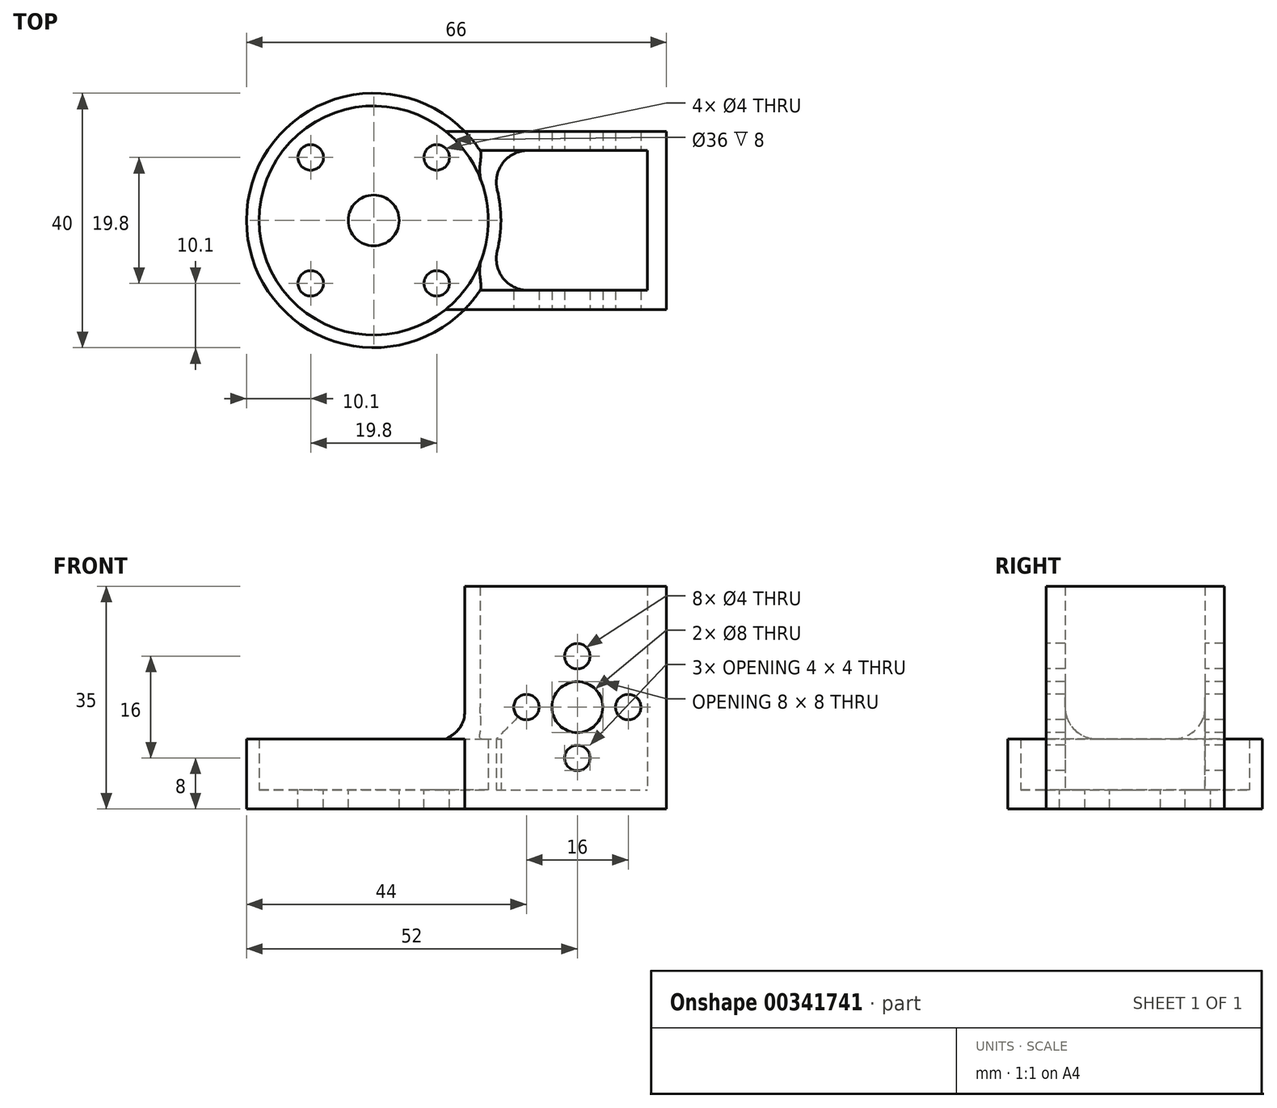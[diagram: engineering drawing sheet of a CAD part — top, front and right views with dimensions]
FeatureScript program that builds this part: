
annotation { "Feature Type Name" : "Feature", "Feature Type Description" : "" }
export const myFeature = defineFeature(function(context is Context, id is Id, definition is map)
    precondition{}
    {
        {
            var Q0;
            Q0=qCreatedBy(makeId("Top.planeOp"),FACE);
            var sketch = newSketch(context, id + "F0", { "sketchPlane" : qUnion([Q0])});
            skCircle(sketch, "E0", {"center": v(0, 0) * mm, "radius": 4 * mm});
            skCircle(sketch, "E1", {"center": v(0, 0) * mm, "radius": 14 * mm, "construction": true});
            skPoint(sketch, "E2", {"position": v(-9.9, 9.9) * mm});
            skLineSegment(sketch, "E3", {"start": v(0, 0) * mm, "end": v(-9.9, 9.9) * mm, "construction": true});
            skPoint(sketch, "E4.MirrorP", {"position": v(-9.9, -9.9) * mm});
            skPoint(sketch, "E5.MirrorP", {"position": v(9.9, 9.9) * mm});
            skPoint(sketch, "E6.MirrorP", {"position": v(9.9, -9.9) * mm});
            skCircle(sketch, "E7", {"center": v(-9.9, 9.9) * mm, "radius": 2 * mm});
            skCircle(sketch, "E8", {"center": v(9.9, 9.9) * mm, "radius": 2 * mm});
            skCircle(sketch, "E9", {"center": v(9.9, -9.9) * mm, "radius": 2 * mm});
            skCircle(sketch, "E10", {"center": v(-9.9, -9.9) * mm, "radius": 2 * mm});
            skCircle(sketch, "E11", {"center": v(0, 0) * mm, "radius": 18 * mm});
            skCircle(sketch, "E12", {"center": v(0, 0) * mm, "radius": 20 * mm});
            skLineSegment(sketch, "E13", {"start": v(46, 14) * mm, "end": v(46, -14) * mm});
            skLineSegment(sketch, "E14", {"start": v(14.28, 14) * mm, "end": v(46, 14) * mm});
            skLineSegment(sketch, "E15", {"start": v(32, 0) * mm, "end": v(0, 0) * mm, "construction": true});
            skLineSegment(sketch, "E16", {"start": v(46, 16) * mm, "end": v(46, -16) * mm, "construction": true});
            skLineSegment(sketch, "E17.MirrorCS", {"start": v(14.28, -14) * mm, "end": v(46, -14) * mm});
            skLineSegment(sketch, "E18.0", {"start": v(16.7, -11) * mm, "end": v(43, -11) * mm});
            skLineSegment(sketch, "E18.1", {"start": v(43, 11) * mm, "end": v(43, -11) * mm});
            skLineSegment(sketch, "E18.2", {"start": v(16.7, 11) * mm, "end": v(43, 11) * mm});
            skSolve(sketch);
        }
        {
            var Q0;
            Q0=makeQuery(id+"F0.imprint","IMPRINT",FACE,{"disambiguationData":[TD([[makeQuery(id+"F0.imprint","IMPRINT",EDGE,{"derivedFrom":sQuery(id+"F0.wireOp",EDGE,"E11")}),-1.0]])]});
            var Q1;
            Q1=makeQuery(id+"F0.imprint","IMPRINT",FACE,{"disambiguationData":[TD([[makeQuery(id+"F0.imprint","IMPRINT",EDGE,{"derivedFrom":sQuery(id+"F0.wireOp",EDGE,"E0")}),-1.0]])]});
            var Q2;
            Q2=makeQuery(id+"F0.imprint","IMPRINT",FACE,{"disambiguationData":[TD([[makeQuery(id+"F0.imprint","IMPRINT",EDGE,{"derivedFrom":sQuery(id+"F0.wireOp",EDGE,"E13")}),-1.0]])]});
            var Q3;
            {var subQ0=sQuery(id+"F0.wireOp",EDGE,"E18.0");Q3=makeQuery(id+"F0.imprint","IMPRINT",FACE,{"disambiguationData":[TD([[makeQuery(id+"F0.imprint","IMPRINT",EDGE,{"derivedFrom":subQ0}),1.0]])]});}
            extrude(context, id + "F1", {"entities" : qUnion([Q0, Q1, Q2, Q3]), "oppositeDirection" : true, "depth" : 3 * mm});
        }
        {
            var Q0;
            Q0=makeQuery(id+"F0.imprint","IMPRINT",FACE,{"disambiguationData":[TD([[makeQuery(id+"F0.imprint","IMPRINT",EDGE,{"derivedFrom":sQuery(id+"F0.wireOp",EDGE,"E11")}),-1.0]])]});
            var Q1;
            Q1=makeQuery(id+"F0.imprint","IMPRINT",FACE,{"disambiguationData":[TD([[makeQuery(id+"F0.imprint","IMPRINT",EDGE,{"derivedFrom":sQuery(id+"F0.wireOp",EDGE,"E13")}),-1.0]])]});
            extrude(context, id + "F2", {"entities" : qUnion([Q0, Q1]), "operationType" : NewBodyOperationType.ADD, "depth" : 8 * mm});
        }
        {
            var Q0;
            Q0=makeQuery(id+"F0.imprint","IMPRINT",FACE,{"disambiguationData":[TD([[makeQuery(id+"F0.imprint","IMPRINT",EDGE,{"derivedFrom":sQuery(id+"F0.wireOp",EDGE,"E13")}),-1.0]])]});
            extrude(context, id + "F3", {"entities" : qUnion([Q0]), "operationType" : NewBodyOperationType.ADD, "depth" : 32 * mm});
        }
        {
            var Q0;
            Q0=qCreatedBy(makeId("Front.planeOp"),FACE);
            var sketch = newSketch(context, id + "F4", { "sketchPlane" : qUnion([Q0])});
            skPoint(sketch, "E19.0", {"position": v(32, 0) * mm});
            skCircle(sketch, "E20", {"center": v(32, 13) * mm, "radius": 4 * mm});
            skCircle(sketch, "E21", {"center": v(32, 5) * mm, "radius": 2 * mm});
            skCircle(sketch, "E22.1.0", {"center": v(40, 13) * mm, "radius": 2 * mm});
            skCircle(sketch, "E22.2.0", {"center": v(32, 21) * mm, "radius": 2 * mm});
            skCircle(sketch, "E22.3.0", {"center": v(24, 13) * mm, "radius": 2 * mm});
            skSolve(sketch);
        }
        {
            var Q0;
            Q0=makeQuery(id+"F4.imprint","IMPRINT",FACE,{"disambiguationData":[TD([[makeQuery(id+"F4.imprint","IMPRINT",EDGE,{"derivedFrom":sQuery(id+"F4.wireOp",EDGE,"E22.2.0")}),1.0]])]});
            var Q1;
            Q1=makeQuery(id+"F4.imprint","IMPRINT",FACE,{"disambiguationData":[TD([[makeQuery(id+"F4.imprint","IMPRINT",EDGE,{"derivedFrom":sQuery(id+"F4.wireOp",EDGE,"E22.3.0")}),1.0]])]});
            var Q2;
            Q2=makeQuery(id+"F4.imprint","IMPRINT",FACE,{"disambiguationData":[TD([[makeQuery(id+"F4.imprint","IMPRINT",EDGE,{"derivedFrom":sQuery(id+"F4.wireOp",EDGE,"E20")}),1.0]])]});
            var Q3;
            Q3=makeQuery(id+"F4.imprint","IMPRINT",FACE,{"disambiguationData":[TD([[makeQuery(id+"F4.imprint","IMPRINT",EDGE,{"derivedFrom":sQuery(id+"F4.wireOp",EDGE,"E22.1.0")}),1.0]])]});
            var Q4;
            Q4=makeQuery(id+"F4.imprint","IMPRINT",FACE,{"disambiguationData":[TD([[makeQuery(id+"F4.imprint","IMPRINT",EDGE,{"derivedFrom":sQuery(id+"F4.wireOp",EDGE,"E21")}),1.0]])]});
            extrude(context, id + "F5", {"entities" : qUnion([Q0, Q1, Q2, Q3, Q4]), "operationType" : NewBodyOperationType.REMOVE, "endBound" : BoundingType.THROUGH_ALL, "oppositeDirection" : true, "depth" : 25 * mm, "hasSecondDirection" : true, "secondDirectionBound" : SecondDirectionBoundingType.THROUGH_ALL, "secondDirectionOppositeDirection" : false, "secondDirectionDepth" : 25 * mm});
        }
        {
            var Q0;
            Q0=makeQuery(id+"F2.opExtrude","SWEPT_EDGE",EDGE,{"disambiguationData":[OSD([sQuery(id+"F0.wireOp",EDGE,"E12"),sQuery(id+"F0.wireOp",EDGE,"E18.2")])]});
            var Q1;
            Q1=makeQuery(id+"F2.opExtrude","SWEPT_EDGE",EDGE,{"disambiguationData":[OSD([sQuery(id+"F0.wireOp",EDGE,"E12"),sQuery(id+"F0.wireOp",EDGE,"E18.0")])]});
            fillet(context, id + "F6", {"entities" : qUnion([Q0, Q1]), "radius" : 5 * mm, "tangentPropagation" : true, "allowEdgeOverflow" : false});
        }
        {
            var Q0;
            {var subQ0=sQuery(id+"F0.wireOp",EDGE,"E17.MirrorCS");var subQ1=sQuery(id+"F0.wireOp",EDGE,"E12");var subQ2=sQuery(id+"F0.wireOp",EDGE,"E18.0");Q0=makeQuery(id+"F3.boolean.opBoolean","INTERSECT",EDGE,{"derivedFrom":[makeQuery(id+"F2.opExtrude","CAP_FACE",FACE,{"disambiguationData":[OSD([sQuery(id+"F0.wireOp",EDGE,"E11"),subQ1,sQuery(id+"F0.wireOp",EDGE,"E13"),sQuery(id+"F0.wireOp",EDGE,"E14"),subQ0,subQ2,sQuery(id+"F0.wireOp",EDGE,"E18.1"),sQuery(id+"F0.wireOp",EDGE,"E18.2")])],"isStart":false}),makeQuery(id+"F3.opExtrude","SWEPT_FACE",FACE,{"disambiguationData":[OSD([subQ1]),TDD([makeQuery(id+"F0.imprint","IMPRINT",EDGE,{"disambiguationData":[TD([[makeQuery(id+"F0.imprint","INTERSECT",VERTEX,{"derivedFrom":[subQ1,subQ0]}),-1.0]])],"derivedFrom":subQ1})])]})]});}
            var Q1;
            Q1=makeQuery(id+"F6.opFillet","TWEAK_EDGE",EDGE,{"derivedFrom":[makeQuery(id+"F2.opExtrude","CAP_VERTEX",VERTEX,{"disambiguationData":[OSD([sQuery(id+"F0.wireOp",EDGE,"E12"),sQuery(id+"F0.wireOp",EDGE,"E18.0")])],"isStart":false})]});
            var Q2;
            {var subQ0=sQuery(id+"F0.wireOp",EDGE,"E14");var subQ1=sQuery(id+"F0.wireOp",EDGE,"E12");var subQ2=sQuery(id+"F0.wireOp",EDGE,"E18.2");Q2=makeQuery(id+"F3.boolean.opBoolean","INTERSECT",EDGE,{"derivedFrom":[makeQuery(id+"F2.opExtrude","CAP_FACE",FACE,{"disambiguationData":[OSD([sQuery(id+"F0.wireOp",EDGE,"E11"),subQ1,sQuery(id+"F0.wireOp",EDGE,"E13"),subQ0,sQuery(id+"F0.wireOp",EDGE,"E17.MirrorCS"),sQuery(id+"F0.wireOp",EDGE,"E18.0"),sQuery(id+"F0.wireOp",EDGE,"E18.1"),subQ2])],"isStart":false}),makeQuery(id+"F3.opExtrude","SWEPT_FACE",FACE,{"disambiguationData":[OSD([subQ1]),TDD([makeQuery(id+"F0.imprint","IMPRINT",EDGE,{"disambiguationData":[TD([[makeQuery(id+"F0.imprint","INTERSECT",VERTEX,{"derivedFrom":[subQ1,subQ0]}),1.0]])],"derivedFrom":subQ1})])]})]});}
            var Q3;
            Q3=makeQuery(id+"F6.opFillet","TWEAK_EDGE",EDGE,{"derivedFrom":[makeQuery(id+"F2.opExtrude","CAP_VERTEX",VERTEX,{"disambiguationData":[OSD([sQuery(id+"F0.wireOp",EDGE,"E12"),sQuery(id+"F0.wireOp",EDGE,"E18.2")])],"isStart":false})]});
            fillet(context, id + "F7", {"entities" : qUnion([Q0, Q1, Q2, Q3]), "radius" : 5 * mm, "tangentPropagation" : true, "allowEdgeOverflow" : false});
        }
    });
